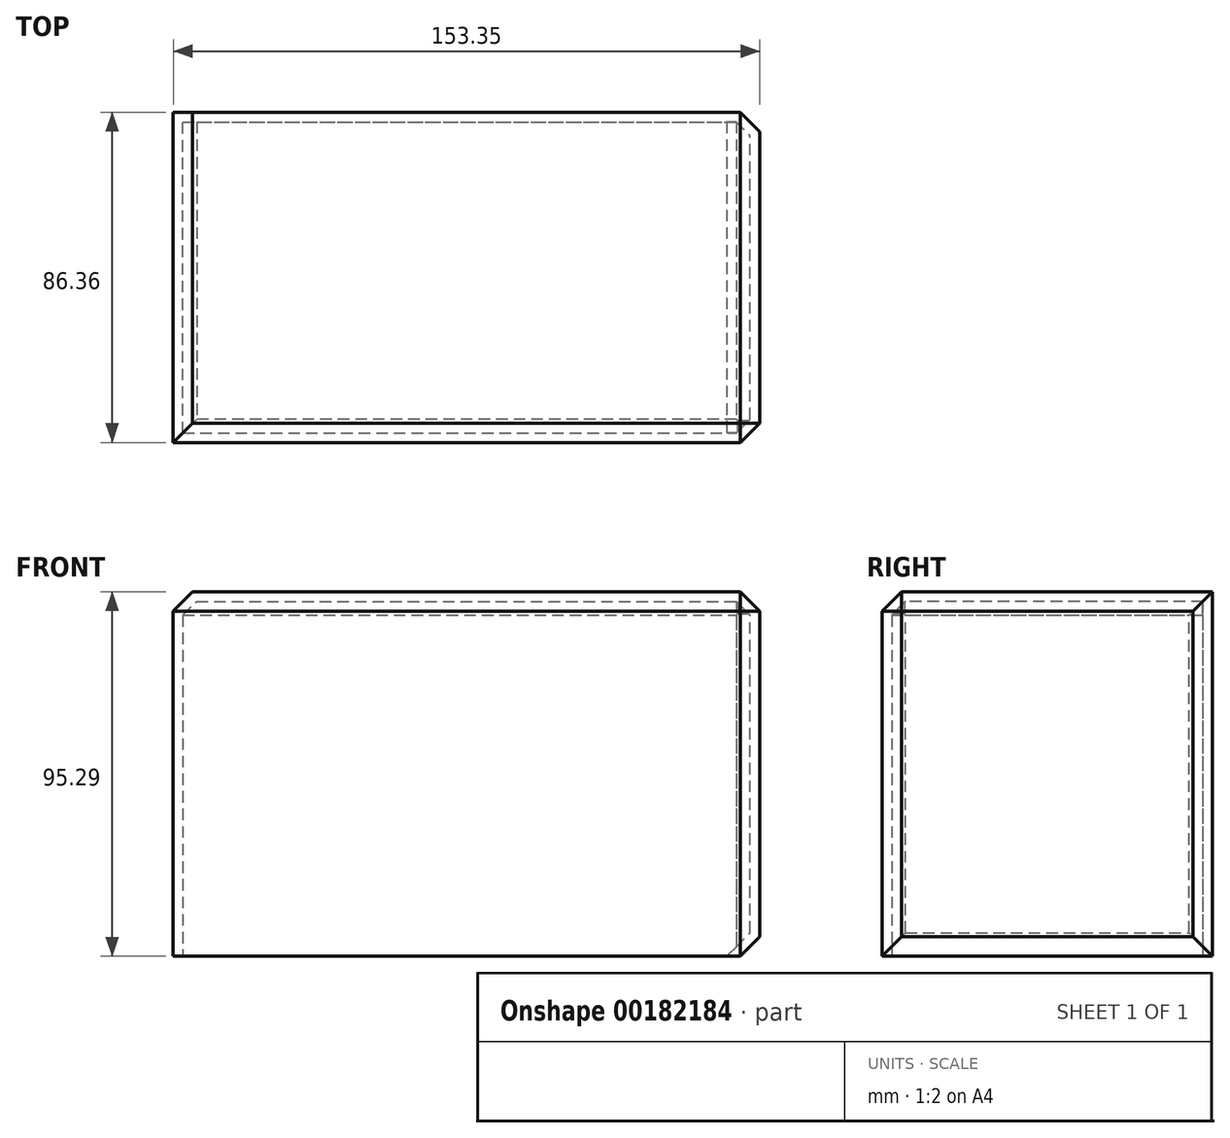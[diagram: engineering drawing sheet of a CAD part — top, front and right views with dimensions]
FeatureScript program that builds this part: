
annotation { "Feature Type Name" : "Feature", "Feature Type Description" : "" }
export const myFeature = defineFeature(function(context is Context, id is Id, definition is map)
    precondition{}
    {
        {
            var Q0;
            Q0=qCreatedBy(makeId("Front.planeOp"),FACE);
            var sketch = newSketch(context, id + "F0", { "sketchPlane" : qUnion([Q0])});
            skLineSegment(sketch, "E0.bottom", {"start": v(-71.37, 53.73) * mm, "end": v(81.98, 53.73) * mm});
            skLineSegment(sketch, "E0.top", {"start": v(-71.37, -41.56) * mm, "end": v(81.98, -41.56) * mm});
            skLineSegment(sketch, "E0.left", {"start": v(-71.37, 53.73) * mm, "end": v(-71.37, -41.56) * mm});
            skLineSegment(sketch, "E0.right", {"start": v(81.98, 53.73) * mm, "end": v(81.98, -41.56) * mm});
            skSolve(sketch);
        }
        {
            var Q0;
            Q0 = qSketchRegion(id + "F0", true);
            extrude(context, id + "F1", {"entities" : qUnion([Q0]), "depth" : 86.36 * mm});
        }
        {
            var Q0;
            Q0=makeQuery(id+"F1.opExtrude","CAP_EDGE",EDGE,{"disambiguationData":[OSD([sQuery(id+"F0.wireOp",EDGE,"E0.bottom")])],"isStart":false});
            var Q1;
            Q1=makeQuery(id+"F1.opExtrude","SWEPT_EDGE",EDGE,{"disambiguationData":[OSD([sQuery(id+"F0.wireOp",EDGE,"E0.bottom"),sQuery(id+"F0.wireOp",EDGE,"E0.right")])]});
            var Q2;
            Q2=makeQuery(id+"F1.opExtrude","SWEPT_EDGE",EDGE,{"disambiguationData":[OSD([sQuery(id+"F0.wireOp",EDGE,"E0.bottom"),sQuery(id+"F0.wireOp",EDGE,"E0.left")])]});
            var Q3;
            Q3=makeQuery(id+"F1.opExtrude","CAP_EDGE",EDGE,{"disambiguationData":[OSD([sQuery(id+"F0.wireOp",EDGE,"E0.right")])],"isStart":false});
            var Q4;
            Q4=makeQuery(id+"F1.opExtrude","CAP_EDGE",EDGE,{"disambiguationData":[OSD([sQuery(id+"F0.wireOp",EDGE,"E0.right")])],"isStart":true});
            var Q5;
            Q5=makeQuery(id+"F1.opExtrude","SWEPT_EDGE",EDGE,{"disambiguationData":[OSD([sQuery(id+"F0.wireOp",EDGE,"E0.top"),sQuery(id+"F0.wireOp",EDGE,"E0.right")])]});
            chamfer(context, id + "F2", {"entities" : qUnion([Q0, Q1, Q2, Q3, Q4, Q5]), "width" : 5.08 * mm, "tangentPropagation" : true});
        }
        {
            var Q0;
            Q0=makeQuery(id+"F1.opExtrude","SWEPT_FACE",FACE,{"disambiguationData":[OSD([sQuery(id+"F0.wireOp",EDGE,"E0.top")])]});
            shell(context, id + "F3", {"entities" : qUnion([Q0]), "thickness" : 2.5 * mm});
        }
    });
